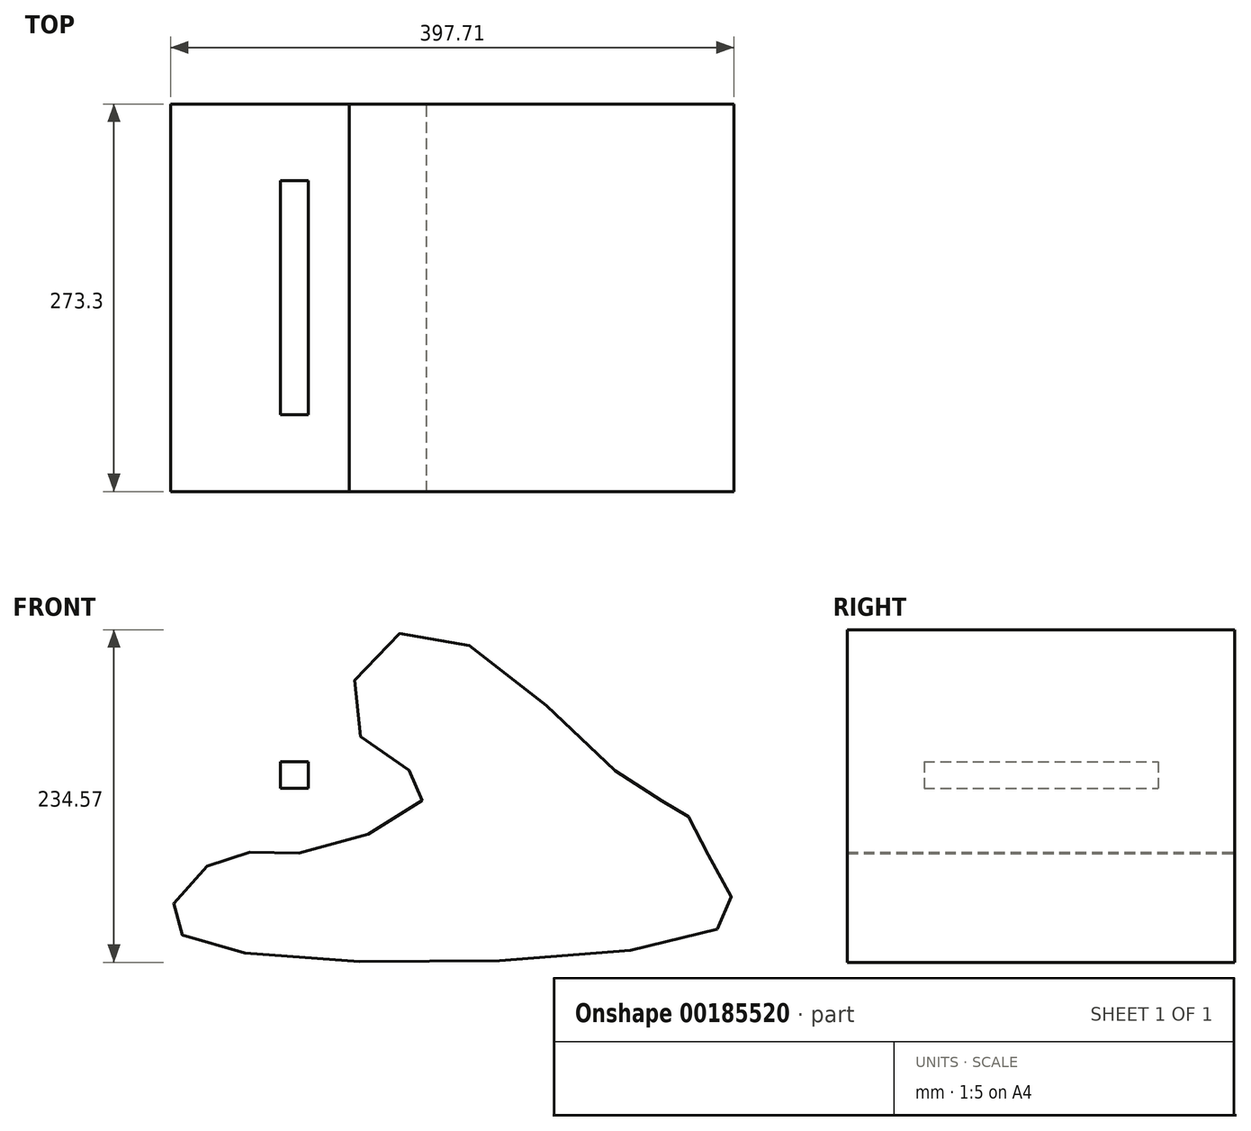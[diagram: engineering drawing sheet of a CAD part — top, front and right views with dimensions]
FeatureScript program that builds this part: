
annotation { "Feature Type Name" : "Feature", "Feature Type Description" : "" }
export const myFeature = defineFeature(function(context is Context, id is Id, definition is map)
    precondition{}
    {
        {
            var Q0;
            Q0=qCreatedBy(makeId("Front.planeOp"),FACE);
            var sketch = newSketch(context, id + "F0", { "sketchPlane" : qUnion([Q0])});
            skFitSpline(sketch, "E0", {"points": [v(0, 0) * mm, v(-51.55, 44.24) * mm, v(-7, 111.82) * mm, v(148.73, 0) * mm, v(181.38, -15.86) * mm, v(203.7, -56.48) * mm, v(213.35, -93.56) * mm, v(-117.21, -117.45) * mm, v(-180.58, -88.3) * mm, v(-141.68, -47.9) * mm, v(-83.21, -44.76) * mm, v(0, 0) * mm]});
            skLineSegment(sketch, "E1.bottom", {"start": v(-130.67, 0) * mm, "end": v(-83.43, 0) * mm});
            skLineSegment(sketch, "E1.top", {"start": v(-130.67, 52.8) * mm, "end": v(-83.43, 52.8) * mm});
            skLineSegment(sketch, "E1.left", {"start": v(-130.67, 0) * mm, "end": v(-130.67, 52.8) * mm});
            skLineSegment(sketch, "E1.right", {"start": v(-83.43, 0) * mm, "end": v(-83.43, 52.8) * mm});
            skLineSegment(sketch, "E2.bottom", {"start": v(-103.11, 18.77) * mm, "end": v(-41.12, 18.77) * mm});
            skLineSegment(sketch, "E2.top", {"start": v(-103.11, -32.3) * mm, "end": v(-41.12, -32.3) * mm});
            skLineSegment(sketch, "E2.left", {"start": v(-103.11, 18.77) * mm, "end": v(-103.11, -32.3) * mm});
            skLineSegment(sketch, "E2.right", {"start": v(-41.12, 18.77) * mm, "end": v(-41.12, -32.3) * mm});
            skSolve(sketch);
        }
        {
            var Q0;
            {var subQ0=sQuery(id+"F0.wireOp",EDGE,"E1.right");var subQ1=sQuery(id+"F0.wireOp",EDGE,"E1.bottom");var subQ2=makeQuery(id+"F0.imprint","INTERSECT",VERTEX,{"derivedFrom":[subQ1,subQ0]});Q0=makeQuery(id+"F0.imprint","IMPRINT",FACE,{"disambiguationData":[TD([[makeQuery(id+"F0.imprint","IMPRINT",EDGE,{"disambiguationData":[TD([[subQ2,1.0]])],"derivedFrom":subQ1}),1.0]])]});}
            extrude(context, id + "F1", {"entities" : qUnion([Q0]), "endBound" : BoundingType.SYMMETRIC, "depth" : 165.1 * mm});
        }
        {
            var Q0;
            Q0=makeQuery(id+"F0.imprint","IMPRINT",FACE,{"disambiguationData":[TD([[makeQuery(id+"F0.imprint","IMPRINT",EDGE,{"derivedFrom":sQuery(id+"F0.wireOp",EDGE,"E0")}),-1.0]])]});
            extrude(context, id + "F2", {"entities" : qUnion([Q0]), "endBound" : BoundingType.SYMMETRIC, "depth" : 273.3 * mm});
        }
    });
